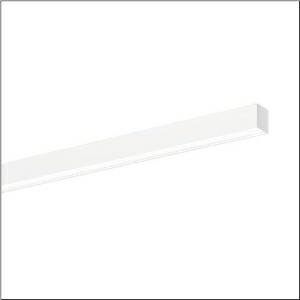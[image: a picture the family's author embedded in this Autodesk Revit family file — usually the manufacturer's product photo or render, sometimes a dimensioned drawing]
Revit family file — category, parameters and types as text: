
# Revit family: silica_21_51mx20da32wb
name_source: partatom
category: Lighting Fixtures
units: mm (PartAtom-declared; Revit-internal decimal feet)

## family parameters
Cut with Voids When Loaded = No
Host = Face
Light Source = No
Part Type = Normal
Room Calculation Point = No
Round Connector Dimension = Use Diameter
Shared = No

## types (1)
- --- (1 x LED, 2400 lm, 16.1 W, 3000K)
    Apparent Load = 16 VA
    CIE Flux Codes = 48 79 96 100 100
    Color Rendering = 80
    Color Temperature = 3000K
    Default Elevation = 1800 mm
    Description = Silica 21, office luminaire, primary optical cover: cover, of PMMA, opal, light emission: direct distribution, primary light characteristic: symmetric, installation type: surface-mounted, LED, rated luminous flux: 2.400lm, luminous efficacy: 149lm/W, light colour: 830, colour temperature: 3000K, control gear: DALI 2, with terminal, 3+2-pole, max. 2.5mm², mains connection: 220..240V, AC, 50/60Hz, rated input power: 16.1W, luminaire housing, of aluminium, traffic white (RAL 9016), length: 1.204mm, width: 53mm, height: 53mm, protection rating (complete): IP20, insulation class (complete): insulation class I (protective earthing), certification: CE, permissible operating ambient temperature: 0..+35°C, standard: EN 50419, packaging unit: 1 piece
    Height = 53 mm
    Lamp = 1 x LED
    Lamp Light Flux = 2400 lm
    Lamp Power = 16.1 W
    Lamp count = 1
    Length = 1204 mm
    Luminous efficacy = 149 lm/W
    Manufacturer = Siteco
    ModVariant = No
    Model = 51MX20DA32WB
    Mounting Place = Ceiling
    Mounting Type = Surface mounted
    Number of Poles = 1
    OnlyDefault = Yes
    Power Factor = 1
    Product Name = Silica 21
    Product group = office luminaire | ceiling mounted
    ProductGroupID = 301
    Protection Class = Protection class I
    Protection Degree = IP 20
    RLX_Detail_Level = 1
    RLX_Emergency_Light_Flux = 0 lm
    RLX_Emergency_Type = 0
    RLX_Emergency_Type_DB = No
    RlxData = <blob elided: 23721 chars, md5=631bf600>
    Socket = socket
    Standby Power = 0 W
    System Light Flux = 2400 lm
    System Power = 16 W
    Type Comments = factory setting: luminous flux: 100 % | dim-lin: 254 | 233 mA
    Type Image = l_1335877.jpg
    URL = http://relux.com
    VarID = @adj_027913
    Voltage = 0 V
    Weight = 0.00 kg
    Width = 53 mm

## geometry (parser evidence)
native form markers: Blend x4, Sweep x10
no freeform markers — native parametric forms only
